# Revit family: MEF-SP-01_RFA
name_source: partatom
category: Aparatos sanitarios
units: mm (PartAtom-declared; Revit-internal decimal feet)

## family parameters
Compartido = No
Corte con vacíos al cargar = No
Cota de conector redondo = Diámetro de uso
Número OmniClass = 23.45.00.00
Punto de cálculo de habitación = No
Se basa en plano de trabajo = No
Siempre vertical = Sí
Tipo de pieza = Normal
Título OmniClass = Sanitary, Laundry, and Cleaning Equipment

## types (1)
- MEF-SP-01
    Brass Chromed = Brass
    Comentarios de tipo = Kitchen Sink Faucets Included Handle
    Descripción = Spacio Kitchen Sink Faucets
    Elevación por defecto = 0"
    Fabricante = HELVEX
    Features = Valvex Left Ceramic Dics; Outlet Rotary
    Inlet Threads = ½" - 14 NPSM
    Max. Working Pressure = 85.3 psi
    Min. Working Pressure = 2.8 psi
    Modelo = MEF-SP-01
    Total Depth = 10"
    Total Height = 13"
    Total Length = 12"

## geometry (parser evidence)
native form markers: Sweep x2
no freeform markers — native parametric forms only
